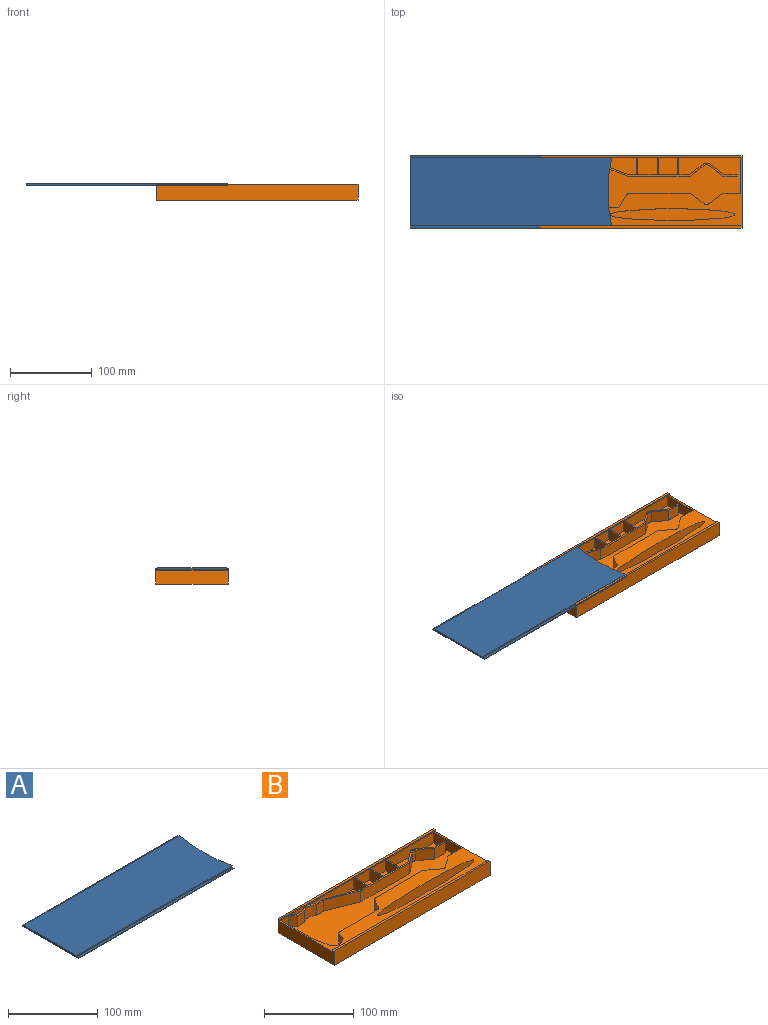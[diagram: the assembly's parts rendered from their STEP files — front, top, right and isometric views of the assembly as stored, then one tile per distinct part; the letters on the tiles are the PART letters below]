
ASSEMBLY  parts=2 mates=1
PART A: 12 faces, bbox 246x89x2.5 mm
  f0: plane 3x0.8mm, normal (1,0,0), area 2.4mm2, adj f4,f6,f7,f11
  f1: plane 246x3mm, normal (0,0,1), area 738mm2, adj f2,f3,f5,f8
  f2: plane 246x0.8mm, normal (0,1,0), area 196.8mm2, adj f1,f3,f5,f7
  f3: plane 89x2.5mm, normal (-1,0,0), area 212.3mm2, adj f1,f2,f4,f6,f7,f8,f9,f10
  f4: plane 246x0.8mm, normal (0,-1,0), area 196.8mm2, adj f0,f3,f6,f7
  f5: plane 3x0.8mm, normal (1,0,0), area 2.4mm2, adj f1,f2,f7,f11
  f6: plane 246x3mm, normal (0,0,1), area 738mm2, adj f0,f3,f4,f9
  f7: plane 246x89mm, normal (0,0,-1), area 21655.1mm2, adj f0,f2,f3,f4,f5,f11
  f8: plane 246x1.7mm, normal (0,1,0), area 418.2mm2, adj f1,f3,f10,f11
  f9: plane 246x1.7mm, normal (0,-1,0), area 418.2mm2, adj f3,f6,f10,f11
  f10: plane 246x83mm, normal (0,0,1), area 20179.1mm2, adj f3,f8,f9,f11
  f11: cylinder r=202.06mm len=83mm, axis (0,0,1), area 209mm2, adj f0,f5,f7,f8,f9,f10
PART B: 71 faces, bbox 246x89x19.5 mm
  f0: plane 246x86.4mm, normal (0,0,1), area 7039.4mm2, adj f2,f4,f6,f7,f8,f9,f10,f11
  f1: plane 246x19.5mm, normal (0,1,0), area 4797mm2, adj f2,f4,f5,f69
  f2: plane 89x19.5mm, normal (-1,0,0), area 1524.6mm2, adj f0,f1,f3,f5,f63,f64,f65,f66
  f3: plane 246x19.5mm, normal (0,-1,0), area 4797mm2, adj f2,f4,f5,f66
  f4: plane 89x19.5mm, normal (1,0,0), area 1524.6mm2, adj f0,f1,f3,f5,f63,f64,f65,f66
  f5: plane 246x89mm, normal (0,0,-1), area 21894mm2, adj f1,f2,f3,f4
  f6: plane 15x12.78mm, normal (0,-1,0), area 191.7mm2, adj f0,f7,f53,f61
  f7: plane 15x6.77mm, normal (-0.7,-0.71,0), area 142.1mm2, adj f0,f6,f8,f61
  f8: plane 15x11.99mm, normal (0,-1,0), area 179.8mm2, adj f0,f7,f9,f61
  f9: cylinder r=14.7mm len=18.86mm, axis (0,0,-1), area 307.2mm2, adj f0,f8,f10,f61
  f10: plane 15x11.27mm, normal (0,-1,0), area 169.1mm2, adj f0,f9,f11,f61
  f11: plane 42.33x16.37mm, normal (-0.36,-0.93,0), area 680.8mm2, adj f0,f10,f12,f61
  f12: plane 76.78x15mm, normal (0,-1,0), area 1151.6mm2, adj f0,f11,f13,f61
  f13: plane 17x15mm, normal (0.6,-0.8,0), area 318.8mm2, adj f0,f12,f14,f61
  f14: cylinder r=5mm len=15mm, axis (0,0,-1), area 96.5mm2, adj f0,f13,f15,f61
  f15: plane 17x15mm, normal (-0.6,-0.8,0), area 318.7mm2, adj f0,f14,f16,f61
  f16: plane 17.33x15mm, normal (0,-1,0), area 259.9mm2, adj f0,f15,f17,f61
  f17: plane 15x2mm, normal (1,0,0), area 30mm2, adj f0,f16,f18,f61
  f18: plane 16.66x15mm, normal (0,1,0), area 249.9mm2, adj f0,f17,f19,f61
  f19: plane 16.47x15mm, normal (0.6,0.8,0), area 308.8mm2, adj f0,f18,f20,f61
  f20: cylinder r=7mm len=15mm, axis (0,0,-1), area 135.1mm2, adj f0,f19,f21,f61
  f21: plane 16.47x15mm, normal (-0.6,0.8,0), area 308.7mm2, adj f0,f20,f22,f61
  f22: plane 15x13.18mm, normal (0,1,0), area 197.7mm2, adj f0,f21,f23,f61
  f23: plane 21x15mm, normal (1,0,0), area 315mm2, adj f0,f22,f24,f61
  f24: plane 75.07x15mm, normal (0,-1,0), area 1126.1mm2, adj f0,f23,f25,f61
  f25: plane 44x15mm, normal (-1,0,0), area 660mm2, adj f0,f24,f26,f61
  f26: plane 21.22x15mm, normal (0,1,0), area 318.4mm2, adj f0,f25,f27,f61
  f27: plane 17x15mm, normal (-0.6,0.8,0), area 318.7mm2, adj f0,f26,f28,f61
  f28: cylinder r=5mm len=15mm, axis (0,0,-1), area 96.5mm2, adj f0,f27,f29,f61
  f29: plane 17x15mm, normal (0.6,0.8,0), area 318.8mm2, adj f0,f28,f30,f61
  f30: plane 73.84x15mm, normal (0,1,0), area 1107.5mm2, adj f0,f29,f31,f61
  f31: cylinder r=5mm len=15mm, axis (0,0,-1), area 79.7mm2, adj f0,f30,f32,f61
  f32: plane 15x12.86mm, normal (-0.87,0.49,0), area 220.7mm2, adj f0,f31,f33,f61
  f33: cylinder r=5mm len=15mm, axis (0,0,-1), area 79.7mm2, adj f0,f32,f34,f61
  f34: plane 59.01x15mm, normal (0,1,0), area 885.1mm2, adj f0,f33,f35,f61
  f35: cylinder r=5mm len=15mm, axis (0,0,-1), area 94.3mm2, adj f0,f34,f36,f61
  f36: plane 15x9.54mm, normal (-0.95,0.31,0), area 150.4mm2, adj f0,f35,f37,f61
  f37: plane 15x10.85mm, normal (-0.44,0.9,0), area 181.2mm2, adj f0,f36,f38,f61
  f38: plane 15x8.19mm, normal (0.54,0.84,0), area 146.5mm2, adj f0,f37,f39,f61
  f39: plane 24.57x15mm, normal (0.98,0.21,0), area 376.7mm2, adj f0,f38,f53,f61
  f40: plane 15x4.81mm, normal (0.69,0.72,0), area 100.1mm2, adj f0,f41,f54,f60
  f41: plane 100.66x15mm, normal (0,-1,0), area 1510mm2, adj f0,f40,f42,f60
  f42: plane 21x15mm, normal (-1,0,0), area 315mm2, adj f0,f41,f43,f60
  f43: plane 15x11.03mm, normal (0,1,0), area 165.4mm2, adj f0,f42,f44,f60
  f44: plane 42.33x16.37mm, normal (0.36,0.93,0), area 680.8mm2, adj f0,f43,f45,f60
  f45: plane 15x10.95mm, normal (0,1,0), area 164.2mm2, adj f0,f44,f46,f60
  f46: cylinder r=16.7mm len=20.26mm, axis (0,0,-1), area 326.6mm2, adj f0,f45,f54,f60
  f47: plane 21x15mm, normal (1,0,0), area 315mm2, adj f0,f48,f55,f59
  f48: plane 23.51x15mm, normal (0,-1,0), area 352.7mm2, adj f0,f47,f49,f59
  f49: plane 21x15mm, normal (-1,0,0), area 315mm2, adj f0,f48,f55,f59
  f50: plane 21x15mm, normal (1,0,0), area 315mm2, adj f0,f51,f56,f58
  f51: plane 23.51x15mm, normal (0,-1,0), area 352.7mm2, adj f0,f50,f52,f58
  f52: plane 21x15mm, normal (-1,0,0), area 315mm2, adj f0,f51,f56,f58
  f53: plane 50.43x15mm, normal (1,0,0), area 756.4mm2, adj f0,f6,f39,f61
  f54: plane 15x11.29mm, normal (0,1,0), area 169.3mm2, adj f0,f40,f46,f60
  f55: plane 23.51x15mm, normal (0,1,0), area 352.7mm2, adj f0,f47,f49,f59
  f56: plane 23.51x15mm, normal (0,1,0), area 352.7mm2, adj f0,f50,f52,f58
  f57: extruded ~152.18x15mm, area 4648.9mm2, adj f0,f62
  f58: plane 23.51x21mm, normal (0,0,1), area 493.7mm2, adj f50,f51,f52,f56
  f59: plane 23.51x21mm, normal (0,0,1), area 493.7mm2, adj f47,f48,f49,f55
  f60: plane 100.66x21mm, normal (0,0,1), area 935mm2, adj f40,f41,f42,f43,f44,f45,f46,f54
  f61: plane 242x80.31mm, normal (0,0,1), area 10566.4mm2, adj f6,f7,f8,f9,f10,f11,f12,f13
  f62: plane 152.18x14.44mm, normal (0,0,1), area 1726.1mm2, adj f57
  f63: plane 246x1mm, normal (0,1,0), area 246mm2, adj f0,f2,f4,f64
  f64: plane 246x1.7mm, normal (0,0,-1), area 418.2mm2, adj f2,f4,f63,f65
  f65: plane 246x1.5mm, normal (0,1,0), area 369mm2, adj f2,f4,f64,f66
  f66: plane 246x3mm, normal (0,0,1), area 738mm2, adj f2,f3,f4,f65
  f67: plane 246x1.7mm, normal (0,0,-1), area 418.2mm2, adj f2,f4,f68,f70
  f68: plane 246x1mm, normal (0,-1,0), area 246mm2, adj f0,f2,f4,f67
  f69: plane 246x3mm, normal (0,0,1), area 738mm2, adj f1,f2,f4,f70
  f70: plane 246x1.5mm, normal (0,-1,0), area 369mm2, adj f2,f4,f67,f69
PLACE A t=(-213.58,120.46,21.93)mm
PLACE B t=(-54.48,-21.8,4.73)mm
MATE slider A.f3 <-> B.f2  axis (-1,0,0) through (-336.58,-63.3,22.73)mm
